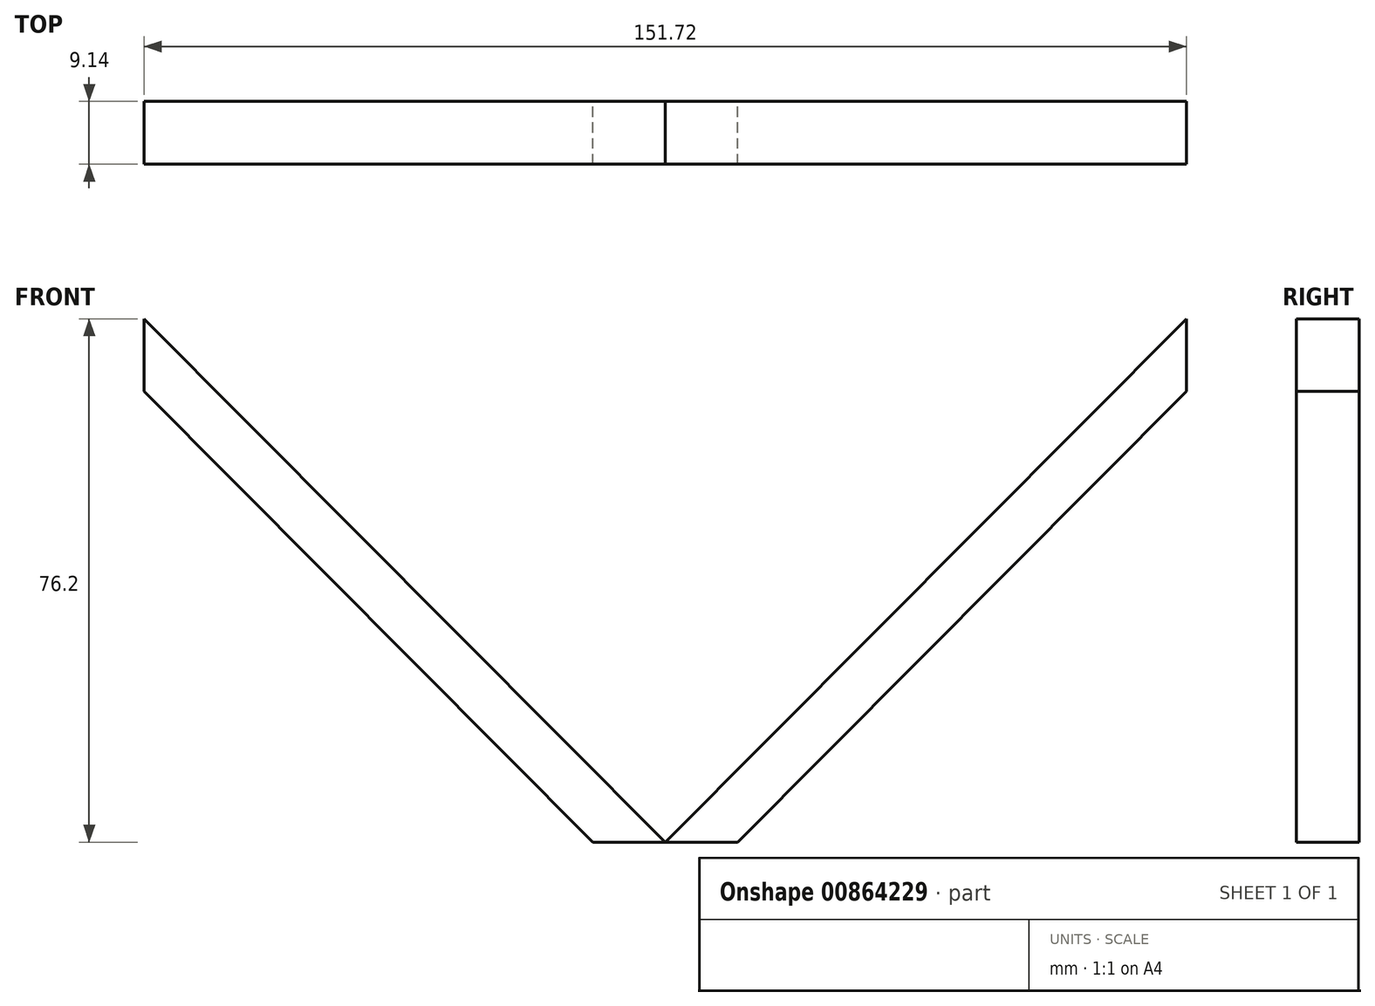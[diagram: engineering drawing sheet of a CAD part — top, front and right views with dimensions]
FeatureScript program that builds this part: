
annotation { "Feature Type Name" : "Feature", "Feature Type Description" : "" }
export const myFeature = defineFeature(function(context is Context, id is Id, definition is map)
    precondition{}
    {
        {
            var Q0;
            Q0=qCreatedBy(makeId("Front.planeOp"),FACE);
            var sketch = newSketch(context, id + "F0", { "sketchPlane" : qUnion([Q0])});
            skLineSegment(sketch, "E0", {"start": v(0, 0) * mm, "end": v(75.86, 76.2) * mm});
            skLineSegment(sketch, "E1", {"start": v(75.86, 76.2) * mm, "end": v(75.86, 65.63) * mm});
            skLineSegment(sketch, "E2", {"start": v(75.86, 65.63) * mm, "end": v(10.53, 0) * mm});
            skLineSegment(sketch, "E3", {"start": v(10.53, 0) * mm, "end": v(0, 0) * mm});
            skLineSegment(sketch, "E4.MirrorCS", {"start": v(-75.86, 65.63) * mm, "end": v(-10.53, 0) * mm});
            skLineSegment(sketch, "E5.MirrorCS", {"start": v(-10.53, 0) * mm, "end": v(0, 0) * mm});
            skLineSegment(sketch, "E6.MirrorCS", {"start": v(0, 0) * mm, "end": v(-75.86, 76.2) * mm});
            skLineSegment(sketch, "E7.MirrorCS", {"start": v(-75.86, 76.2) * mm, "end": v(-75.86, 65.63) * mm});
            skSolve(sketch);
        }
        {
            var Q0;
            Q0=makeQuery(id+"F0.imprint","IMPRINT",FACE,{"disambiguationData":[TD([[makeQuery(id+"F0.imprint","IMPRINT",EDGE,{"derivedFrom":sQuery(id+"F0.wireOp",EDGE,"E4.MirrorCS")}),1.0]])]});
            var Q1;
            Q1=makeQuery(id+"F0.imprint","IMPRINT",FACE,{"disambiguationData":[TD([[makeQuery(id+"F0.imprint","IMPRINT",EDGE,{"derivedFrom":sQuery(id+"F0.wireOp",EDGE,"E0")}),-1.0]])]});
            extrude(context, id + "F1", {"entities" : qUnion([Q0, Q1]), "depth" : 9.14 * mm, "offsetDistance" : 25.4 * mm});
        }
    });
